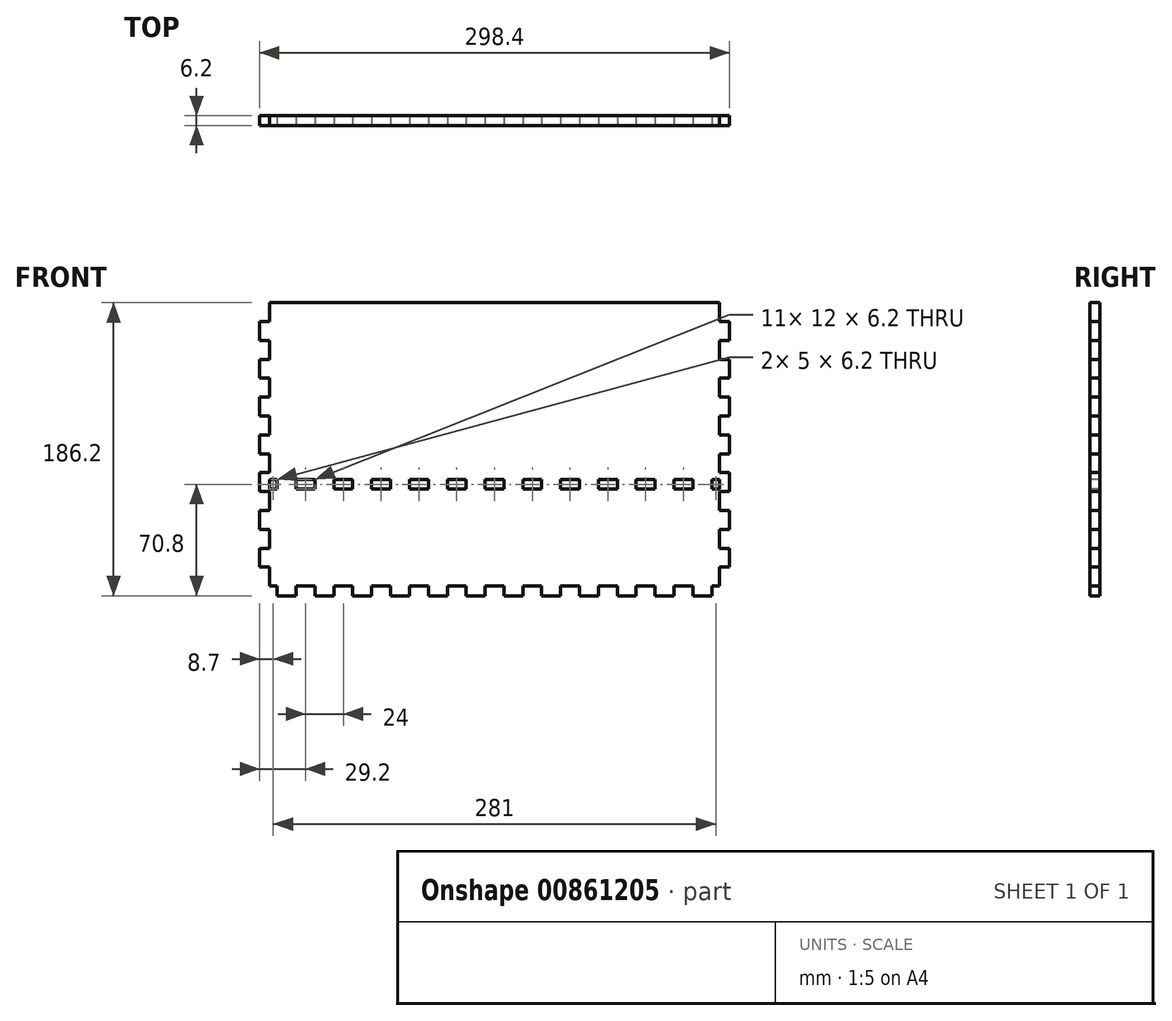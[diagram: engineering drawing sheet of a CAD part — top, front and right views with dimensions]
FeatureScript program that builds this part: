
annotation { "Feature Type Name" : "Feature", "Feature Type Description" : "" }
export const myFeature = defineFeature(function(context is Context, id is Id, definition is map)
    precondition{}
    {
        {
            var Q0;
            Q0=qCreatedBy(makeId("Front.planeOp"),FACE);
            var sketch = newSketch(context, id + "F0", { "sketchPlane" : qUnion([Q0])});
            skLineSegment(sketch, "E0.bottom", {"start": v(143, 90) * mm, "end": v(-143, 90) * mm});
            skLineSegment(sketch, "E0.top", {"start": v(143, -90) * mm, "end": v(-143, -90) * mm});
            skLineSegment(sketch, "E0.left", {"start": v(143, 90) * mm, "end": v(143, -90) * mm});
            skLineSegment(sketch, "E0.right", {"start": v(-143, 90) * mm, "end": v(-143, -90) * mm});
            skPoint(sketch, "E0.middle", {"position": v(0, 0) * mm});
            skSolve(sketch);
        }
        {
            var Q0;
            Q0=makeQuery(id+"F0.imprint","IMPRINT",FACE,{"disambiguationData":[TD([[makeQuery(id+"F0.imprint","IMPRINT",EDGE,{"derivedFrom":sQuery(id+"F0.wireOp",EDGE,"E0.bottom")}),1.0]])]});
            extrude(context, id + "F1", {"entities" : qUnion([Q0]), "depth" : 6.2 * mm, "offsetDistance" : 25 * mm});
        }
        {
            var Q0;
            Q0=makeQuery(id+"F1.opExtrude","CAP_FACE",FACE,{"disambiguationData":[OSD([sQuery(id+"F0.wireOp",EDGE,"E0.bottom"),sQuery(id+"F0.wireOp",EDGE,"E0.top"),sQuery(id+"F0.wireOp",EDGE,"E0.left"),sQuery(id+"F0.wireOp",EDGE,"E0.right")])],"isStart":false});
            var sketch = newSketch(context, id + "F2", { "sketchPlane" : qUnion([Q0])});
            skLineSegment(sketch, "E1", {"start": v(-143, -90) * mm, "end": v(-143, -28.5) * mm, "construction": true});
            skLineSegment(sketch, "E2", {"start": v(-143, -28.5) * mm, "end": v(0, -28.5) * mm, "construction": true});
            skLineSegment(sketch, "E3", {"start": v(0, -28.5) * mm, "end": v(0, -22.3) * mm, "construction": true});
            skLineSegment(sketch, "E4.bottom", {"start": v(6, -22.3) * mm, "end": v(-6, -22.3) * mm});
            skLineSegment(sketch, "E4.top", {"start": v(6, -28.5) * mm, "end": v(-6, -28.5) * mm});
            skLineSegment(sketch, "E4.left", {"start": v(6, -22.3) * mm, "end": v(6, -28.5) * mm});
            skLineSegment(sketch, "E4.right", {"start": v(-6, -22.3) * mm, "end": v(-6, -28.5) * mm});
            skPoint(sketch, "E4.middle", {"position": v(0, -25.4) * mm});
            skLineSegment(sketch, "E5.1.0.0", {"start": v(30, -22.3) * mm, "end": v(18, -22.3) * mm});
            skLineSegment(sketch, "E5.1.0.1", {"start": v(30, -22.3) * mm, "end": v(30, -28.5) * mm});
            skLineSegment(sketch, "E5.1.0.2", {"start": v(30, -28.5) * mm, "end": v(18, -28.5) * mm});
            skLineSegment(sketch, "E5.1.0.3", {"start": v(18, -22.3) * mm, "end": v(18, -28.5) * mm});
            skLineSegment(sketch, "E5.2.0.0", {"start": v(54, -22.3) * mm, "end": v(42, -22.3) * mm});
            skLineSegment(sketch, "E5.2.0.1", {"start": v(54, -22.3) * mm, "end": v(54, -28.5) * mm});
            skLineSegment(sketch, "E5.2.0.2", {"start": v(54, -28.5) * mm, "end": v(42, -28.5) * mm});
            skLineSegment(sketch, "E5.2.0.3", {"start": v(42, -22.3) * mm, "end": v(42, -28.5) * mm});
            skLineSegment(sketch, "E5.3.0.0", {"start": v(78, -22.3) * mm, "end": v(66, -22.3) * mm});
            skLineSegment(sketch, "E5.3.0.1", {"start": v(78, -22.3) * mm, "end": v(78, -28.5) * mm});
            skLineSegment(sketch, "E5.3.0.2", {"start": v(78, -28.5) * mm, "end": v(66, -28.5) * mm});
            skLineSegment(sketch, "E5.3.0.3", {"start": v(66, -22.3) * mm, "end": v(66, -28.5) * mm});
            skLineSegment(sketch, "E5.4.0.0", {"start": v(102, -22.3) * mm, "end": v(90, -22.3) * mm});
            skLineSegment(sketch, "E5.4.0.1", {"start": v(102, -22.3) * mm, "end": v(102, -28.5) * mm});
            skLineSegment(sketch, "E5.4.0.2", {"start": v(102, -28.5) * mm, "end": v(90, -28.5) * mm});
            skLineSegment(sketch, "E5.4.0.3", {"start": v(90, -22.3) * mm, "end": v(90, -28.5) * mm});
            skLineSegment(sketch, "E5.5.0.0", {"start": v(126, -22.3) * mm, "end": v(114, -22.3) * mm});
            skLineSegment(sketch, "E5.5.0.1", {"start": v(126, -22.3) * mm, "end": v(126, -28.5) * mm});
            skLineSegment(sketch, "E5.5.0.2", {"start": v(126, -28.5) * mm, "end": v(114, -28.5) * mm});
            skLineSegment(sketch, "E5.5.0.3", {"start": v(114, -22.3) * mm, "end": v(114, -28.5) * mm});
            skLineSegment(sketch, "E5.direction1", {"start": v(-6, -22.3) * mm, "end": v(18, -22.3) * mm, "construction": true});
            skLineSegment(sketch, "E6.MirrorCS", {"start": v(-78, -22.3) * mm, "end": v(-78, -28.5) * mm});
            skLineSegment(sketch, "E7.MirrorCS", {"start": v(-66, -22.3) * mm, "end": v(-66, -28.5) * mm});
            skLineSegment(sketch, "E8.MirrorCS", {"start": v(-102, -22.3) * mm, "end": v(-102, -28.5) * mm});
            skLineSegment(sketch, "E9.MirrorCS", {"start": v(-90, -22.3) * mm, "end": v(-90, -28.5) * mm});
            skLineSegment(sketch, "E10.MirrorCS", {"start": v(-54, -22.3) * mm, "end": v(-54, -28.5) * mm});
            skLineSegment(sketch, "E11.MirrorCS", {"start": v(-42, -22.3) * mm, "end": v(-42, -28.5) * mm});
            skLineSegment(sketch, "E12.MirrorCS", {"start": v(-126, -22.3) * mm, "end": v(-126, -28.5) * mm});
            skLineSegment(sketch, "E13.MirrorCS", {"start": v(-18, -22.3) * mm, "end": v(-18, -28.5) * mm});
            skLineSegment(sketch, "E14.MirrorCS", {"start": v(-30, -22.3) * mm, "end": v(-30, -28.5) * mm});
            skLineSegment(sketch, "E15.MirrorCS", {"start": v(-114, -22.3) * mm, "end": v(-114, -28.5) * mm});
            skLineSegment(sketch, "E16.MirrorCS", {"start": v(-78, -28.5) * mm, "end": v(-66, -28.5) * mm});
            skLineSegment(sketch, "E17.MirrorCS", {"start": v(-102, -22.3) * mm, "end": v(-90, -22.3) * mm});
            skLineSegment(sketch, "E18.MirrorCS", {"start": v(-102, -28.5) * mm, "end": v(-90, -28.5) * mm});
            skLineSegment(sketch, "E19.MirrorCS", {"start": v(-126, -22.3) * mm, "end": v(-114, -22.3) * mm});
            skLineSegment(sketch, "E20.MirrorCS", {"start": v(-54, -22.3) * mm, "end": v(-42, -22.3) * mm});
            skLineSegment(sketch, "E21.MirrorCS", {"start": v(-54, -28.5) * mm, "end": v(-42, -28.5) * mm});
            skLineSegment(sketch, "E22.MirrorCS", {"start": v(-78, -22.3) * mm, "end": v(-66, -22.3) * mm});
            skLineSegment(sketch, "E23.MirrorCS", {"start": v(-126, -28.5) * mm, "end": v(-114, -28.5) * mm});
            skLineSegment(sketch, "E24.MirrorCS", {"start": v(-30, -22.3) * mm, "end": v(-18, -22.3) * mm});
            skLineSegment(sketch, "E25.MirrorCS", {"start": v(-30, -28.5) * mm, "end": v(-18, -28.5) * mm});
            skLineSegment(sketch, "E26.0.6.0", {"start": v(150, -22.3) * mm, "end": v(138, -22.3) * mm});
            skLineSegment(sketch, "E26.3.6.0", {"start": v(150, -22.3) * mm, "end": v(150, -28.5) * mm});
            skLineSegment(sketch, "E26.6.6.0", {"start": v(150, -28.5) * mm, "end": v(138, -28.5) * mm});
            skLineSegment(sketch, "E26.9.6.0", {"start": v(138, -22.3) * mm, "end": v(138, -28.5) * mm});
            skLineSegment(sketch, "E27.MirrorCS", {"start": v(-150, -22.3) * mm, "end": v(-138, -22.3) * mm});
            skLineSegment(sketch, "E28.MirrorCS", {"start": v(-150, -28.5) * mm, "end": v(-138, -28.5) * mm});
            skLineSegment(sketch, "E29.MirrorCS", {"start": v(-138, -22.3) * mm, "end": v(-138, -28.5) * mm});
            skLineSegment(sketch, "E30.MirrorCS", {"start": v(-150, -22.3) * mm, "end": v(-150, -28.5) * mm});
            skSolve(sketch);
        }
        {
            var Q0;
            Q0=makeQuery(id+"F2.imprint","IMPRINT",FACE,{"disambiguationData":[TD([[makeQuery(id+"F2.imprint","IMPRINT",EDGE,{"derivedFrom":sQuery(id+"F2.wireOp",EDGE,"E12.MirrorCS")}),1.0]])]});
            var Q1;
            Q1=makeQuery(id+"F2.imprint","IMPRINT",FACE,{"disambiguationData":[TD([[makeQuery(id+"F2.imprint","IMPRINT",EDGE,{"derivedFrom":sQuery(id+"F2.wireOp",EDGE,"E8.MirrorCS")}),1.0]])]});
            var Q2;
            Q2=makeQuery(id+"F2.imprint","IMPRINT",FACE,{"disambiguationData":[TD([[makeQuery(id+"F2.imprint","IMPRINT",EDGE,{"derivedFrom":sQuery(id+"F2.wireOp",EDGE,"E6.MirrorCS")}),1.0]])]});
            var Q3;
            Q3=makeQuery(id+"F2.imprint","IMPRINT",FACE,{"disambiguationData":[TD([[makeQuery(id+"F2.imprint","IMPRINT",EDGE,{"derivedFrom":sQuery(id+"F2.wireOp",EDGE,"E10.MirrorCS")}),1.0]])]});
            var Q4;
            Q4=makeQuery(id+"F2.imprint","IMPRINT",FACE,{"disambiguationData":[TD([[makeQuery(id+"F2.imprint","IMPRINT",EDGE,{"derivedFrom":sQuery(id+"F2.wireOp",EDGE,"E13.MirrorCS")}),-1.0]])]});
            var Q5;
            Q5=makeQuery(id+"F2.imprint","IMPRINT",FACE,{"disambiguationData":[TD([[makeQuery(id+"F2.imprint","IMPRINT",EDGE,{"derivedFrom":sQuery(id+"F2.wireOp",EDGE,"E4.bottom")}),1.0]])]});
            var Q6;
            Q6=makeQuery(id+"F2.imprint","IMPRINT",FACE,{"disambiguationData":[TD([[makeQuery(id+"F2.imprint","IMPRINT",EDGE,{"derivedFrom":sQuery(id+"F2.wireOp",EDGE,"E5.1.0.0")}),1.0]])]});
            var Q7;
            Q7=makeQuery(id+"F2.imprint","IMPRINT",FACE,{"disambiguationData":[TD([[makeQuery(id+"F2.imprint","IMPRINT",EDGE,{"derivedFrom":sQuery(id+"F2.wireOp",EDGE,"E5.2.0.0")}),1.0]])]});
            var Q8;
            Q8=makeQuery(id+"F2.imprint","IMPRINT",FACE,{"disambiguationData":[TD([[makeQuery(id+"F2.imprint","IMPRINT",EDGE,{"derivedFrom":sQuery(id+"F2.wireOp",EDGE,"E5.3.0.0")}),1.0]])]});
            var Q9;
            Q9=makeQuery(id+"F2.imprint","IMPRINT",FACE,{"disambiguationData":[TD([[makeQuery(id+"F2.imprint","IMPRINT",EDGE,{"derivedFrom":sQuery(id+"F2.wireOp",EDGE,"E5.4.0.0")}),1.0]])]});
            var Q10;
            Q10=makeQuery(id+"F2.imprint","IMPRINT",FACE,{"disambiguationData":[TD([[makeQuery(id+"F2.imprint","IMPRINT",EDGE,{"derivedFrom":sQuery(id+"F2.wireOp",EDGE,"E5.5.0.0")}),1.0]])]});
            var Q11;
            {var subQ0=sQuery(id+"F2.wireOp",EDGE,"E29.MirrorCS");Q11=makeQuery(id+"F2.imprint","IMPRINT",FACE,{"disambiguationData":[TD([[makeQuery(id+"F2.imprint","IMPRINT",EDGE,{"derivedFrom":subQ0}),-1.0]])]});}
            var Q12;
            {var subQ0=sQuery(id+"F2.wireOp",EDGE,"E26.9.6.0");Q12=makeQuery(id+"F2.imprint","IMPRINT",FACE,{"disambiguationData":[TD([[makeQuery(id+"F2.imprint","IMPRINT",EDGE,{"derivedFrom":subQ0}),1.0]])]});}
            extrude(context, id + "F3", {"entities" : qUnion([Q0, Q1, Q2, Q3, Q4, Q5, Q6, Q7, Q8, Q9, Q10, Q11, Q12]), "operationType" : NewBodyOperationType.REMOVE, "endBound" : BoundingType.THROUGH_ALL, "oppositeDirection" : true, "depth" : 25 * mm, "offsetDistance" : 25 * mm});
        }
        {
            var Q0;
            Q0=makeQuery(id+"F1.opExtrude","CAP_FACE",FACE,{"disambiguationData":[OSD([sQuery(id+"F0.wireOp",EDGE,"E0.bottom"),sQuery(id+"F0.wireOp",EDGE,"E0.top"),sQuery(id+"F0.wireOp",EDGE,"E0.left"),sQuery(id+"F0.wireOp",EDGE,"E0.right")])],"isStart":false});
            var sketch = newSketch(context, id + "F4", { "sketchPlane" : qUnion([Q0])});
            skLineSegment(sketch, "E31", {"start": v(0, -90) * mm, "end": v(6, -90) * mm, "construction": true});
            skLineSegment(sketch, "E32.bottom", {"start": v(6, -90) * mm, "end": v(18, -90) * mm});
            skLineSegment(sketch, "E32.top", {"start": v(6, -96.2) * mm, "end": v(18, -96.2) * mm});
            skLineSegment(sketch, "E32.left", {"start": v(6, -90) * mm, "end": v(6, -96.2) * mm});
            skLineSegment(sketch, "E32.right", {"start": v(18, -90) * mm, "end": v(18, -96.2) * mm});
            skLineSegment(sketch, "E33.1.0.0", {"start": v(30, -96.2) * mm, "end": v(42, -96.2) * mm});
            skLineSegment(sketch, "E33.1.0.1", {"start": v(42, -90) * mm, "end": v(42, -96.2) * mm});
            skLineSegment(sketch, "E33.1.0.2", {"start": v(30, -90) * mm, "end": v(42, -90) * mm});
            skLineSegment(sketch, "E33.1.0.3", {"start": v(30, -90) * mm, "end": v(30, -96.2) * mm});
            skLineSegment(sketch, "E33.1.0.4", {"start": v(24, -90) * mm, "end": v(30, -90) * mm, "construction": true});
            skLineSegment(sketch, "E33.2.0.0", {"start": v(54, -96.2) * mm, "end": v(66, -96.2) * mm});
            skLineSegment(sketch, "E33.2.0.1", {"start": v(66, -90) * mm, "end": v(66, -96.2) * mm});
            skLineSegment(sketch, "E33.2.0.2", {"start": v(54, -90) * mm, "end": v(66, -90) * mm});
            skLineSegment(sketch, "E33.2.0.3", {"start": v(54, -90) * mm, "end": v(54, -96.2) * mm});
            skLineSegment(sketch, "E33.2.0.4", {"start": v(48, -90) * mm, "end": v(54, -90) * mm, "construction": true});
            skLineSegment(sketch, "E33.3.0.0", {"start": v(78, -96.2) * mm, "end": v(90, -96.2) * mm});
            skLineSegment(sketch, "E33.3.0.1", {"start": v(90, -90) * mm, "end": v(90, -96.2) * mm});
            skLineSegment(sketch, "E33.3.0.2", {"start": v(78, -90) * mm, "end": v(90, -90) * mm});
            skLineSegment(sketch, "E33.3.0.3", {"start": v(78, -90) * mm, "end": v(78, -96.2) * mm});
            skLineSegment(sketch, "E33.3.0.4", {"start": v(72, -90) * mm, "end": v(78, -90) * mm, "construction": true});
            skLineSegment(sketch, "E33.4.0.0", {"start": v(102, -96.2) * mm, "end": v(114, -96.2) * mm});
            skLineSegment(sketch, "E33.4.0.1", {"start": v(114, -90) * mm, "end": v(114, -96.2) * mm});
            skLineSegment(sketch, "E33.4.0.2", {"start": v(102, -90) * mm, "end": v(114, -90) * mm});
            skLineSegment(sketch, "E33.4.0.3", {"start": v(102, -90) * mm, "end": v(102, -96.2) * mm});
            skLineSegment(sketch, "E33.4.0.4", {"start": v(96, -90) * mm, "end": v(102, -90) * mm, "construction": true});
            skLineSegment(sketch, "E33.5.0.0", {"start": v(126, -96.2) * mm, "end": v(138, -96.2) * mm});
            skLineSegment(sketch, "E33.5.0.1", {"start": v(138, -90) * mm, "end": v(138, -96.2) * mm});
            skLineSegment(sketch, "E33.5.0.2", {"start": v(126, -90) * mm, "end": v(138, -90) * mm});
            skLineSegment(sketch, "E33.5.0.3", {"start": v(126, -90) * mm, "end": v(126, -96.2) * mm});
            skLineSegment(sketch, "E33.5.0.4", {"start": v(120, -90) * mm, "end": v(126, -90) * mm, "construction": true});
            skLineSegment(sketch, "E33.direction1", {"start": v(6, -96.2) * mm, "end": v(30, -96.2) * mm, "construction": true});
            skLineSegment(sketch, "E34.MirrorCS", {"start": v(-6, -90) * mm, "end": v(-6, -96.2) * mm});
            skLineSegment(sketch, "E35.MirrorCS", {"start": v(-30, -90) * mm, "end": v(-30, -96.2) * mm});
            skLineSegment(sketch, "E36.MirrorCS", {"start": v(-42, -90) * mm, "end": v(-42, -96.2) * mm});
            skLineSegment(sketch, "E37.MirrorCS", {"start": v(-78, -90) * mm, "end": v(-78, -96.2) * mm});
            skLineSegment(sketch, "E38.MirrorCS", {"start": v(-18, -90) * mm, "end": v(-18, -96.2) * mm});
            skLineSegment(sketch, "E39.MirrorCS", {"start": v(-114, -90) * mm, "end": v(-114, -96.2) * mm});
            skLineSegment(sketch, "E40.MirrorCS", {"start": v(-102, -90) * mm, "end": v(-102, -96.2) * mm});
            skLineSegment(sketch, "E41.MirrorCS", {"start": v(-66, -90) * mm, "end": v(-66, -96.2) * mm});
            skLineSegment(sketch, "E42.MirrorCS", {"start": v(-54, -90) * mm, "end": v(-54, -96.2) * mm});
            skLineSegment(sketch, "E43.MirrorCS", {"start": v(-138, -90) * mm, "end": v(-138, -96.2) * mm});
            skLineSegment(sketch, "E44.MirrorCS", {"start": v(-126, -90) * mm, "end": v(-126, -96.2) * mm});
            skLineSegment(sketch, "E45.MirrorCS", {"start": v(-90, -90) * mm, "end": v(-90, -96.2) * mm});
            skLineSegment(sketch, "E46.MirrorCS", {"start": v(-72, -90) * mm, "end": v(-78, -90) * mm, "construction": true});
            skLineSegment(sketch, "E47.MirrorCS", {"start": v(-120, -90) * mm, "end": v(-126, -90) * mm, "construction": true});
            skLineSegment(sketch, "E48.MirrorCS", {"start": v(-6, -96.2) * mm, "end": v(-18, -96.2) * mm});
            skLineSegment(sketch, "E49.MirrorCS", {"start": v(-96, -90) * mm, "end": v(-102, -90) * mm, "construction": true});
            skLineSegment(sketch, "E50.MirrorCS", {"start": v(-48, -90) * mm, "end": v(-54, -90) * mm, "construction": true});
            skLineSegment(sketch, "E51.MirrorCS", {"start": v(-24, -90) * mm, "end": v(-30, -90) * mm, "construction": true});
            skLineSegment(sketch, "E52.MirrorCS", {"start": v(-78, -90) * mm, "end": v(-90, -90) * mm});
            skLineSegment(sketch, "E53.MirrorCS", {"start": v(-30, -96.2) * mm, "end": v(-42, -96.2) * mm});
            skLineSegment(sketch, "E54.MirrorCS", {"start": v(-102, -96.2) * mm, "end": v(-114, -96.2) * mm});
            skLineSegment(sketch, "E55.MirrorCS", {"start": v(-6, -96.2) * mm, "end": v(-30, -96.2) * mm, "construction": true});
            skLineSegment(sketch, "E56.MirrorCS", {"start": v(-6, -90) * mm, "end": v(-18, -90) * mm});
            skLineSegment(sketch, "E57.MirrorCS", {"start": v(-102, -90) * mm, "end": v(-114, -90) * mm});
            skLineSegment(sketch, "E58.MirrorCS", {"start": v(-54, -90) * mm, "end": v(-66, -90) * mm});
            skLineSegment(sketch, "E59.MirrorCS", {"start": v(-126, -96.2) * mm, "end": v(-138, -96.2) * mm});
            skLineSegment(sketch, "E60.MirrorCS", {"start": v(-54, -96.2) * mm, "end": v(-66, -96.2) * mm});
            skLineSegment(sketch, "E61.MirrorCS", {"start": v(-126, -90) * mm, "end": v(-138, -90) * mm});
            skLineSegment(sketch, "E62.MirrorCS", {"start": v(-78, -96.2) * mm, "end": v(-90, -96.2) * mm});
            skLineSegment(sketch, "E63.MirrorCS", {"start": v(-30, -90) * mm, "end": v(-42, -90) * mm});
            skSolve(sketch);
        }
        {
            var Q0;
            Q0=makeQuery(id+"F4.imprint","IMPRINT",FACE,{"disambiguationData":[TD([[makeQuery(id+"F4.imprint","IMPRINT",EDGE,{"derivedFrom":sQuery(id+"F4.wireOp",EDGE,"E43.MirrorCS")}),1.0]])]});
            var Q1;
            Q1=makeQuery(id+"F4.imprint","IMPRINT",FACE,{"disambiguationData":[TD([[makeQuery(id+"F4.imprint","IMPRINT",EDGE,{"derivedFrom":sQuery(id+"F4.wireOp",EDGE,"E39.MirrorCS")}),1.0]])]});
            var Q2;
            Q2=makeQuery(id+"F4.imprint","IMPRINT",FACE,{"disambiguationData":[TD([[makeQuery(id+"F4.imprint","IMPRINT",EDGE,{"derivedFrom":sQuery(id+"F4.wireOp",EDGE,"E37.MirrorCS")}),-1.0]])]});
            var Q3;
            Q3=makeQuery(id+"F4.imprint","IMPRINT",FACE,{"disambiguationData":[TD([[makeQuery(id+"F4.imprint","IMPRINT",EDGE,{"derivedFrom":sQuery(id+"F4.wireOp",EDGE,"E41.MirrorCS")}),1.0]])]});
            var Q4;
            Q4=makeQuery(id+"F4.imprint","IMPRINT",FACE,{"disambiguationData":[TD([[makeQuery(id+"F4.imprint","IMPRINT",EDGE,{"derivedFrom":sQuery(id+"F4.wireOp",EDGE,"E35.MirrorCS")}),-1.0]])]});
            var Q5;
            Q5=makeQuery(id+"F4.imprint","IMPRINT",FACE,{"disambiguationData":[TD([[makeQuery(id+"F4.imprint","IMPRINT",EDGE,{"derivedFrom":sQuery(id+"F4.wireOp",EDGE,"E34.MirrorCS")}),-1.0]])]});
            var Q6;
            Q6=makeQuery(id+"F4.imprint","IMPRINT",FACE,{"disambiguationData":[TD([[makeQuery(id+"F4.imprint","IMPRINT",EDGE,{"derivedFrom":sQuery(id+"F4.wireOp",EDGE,"E32.bottom")}),1.0]])]});
            var Q7;
            Q7=makeQuery(id+"F4.imprint","IMPRINT",FACE,{"disambiguationData":[TD([[makeQuery(id+"F4.imprint","IMPRINT",EDGE,{"derivedFrom":sQuery(id+"F4.wireOp",EDGE,"E33.1.0.0")}),1.0]])]});
            var Q8;
            Q8=makeQuery(id+"F4.imprint","IMPRINT",FACE,{"disambiguationData":[TD([[makeQuery(id+"F4.imprint","IMPRINT",EDGE,{"derivedFrom":sQuery(id+"F4.wireOp",EDGE,"E33.2.0.0")}),1.0]])]});
            var Q9;
            Q9=makeQuery(id+"F4.imprint","IMPRINT",FACE,{"disambiguationData":[TD([[makeQuery(id+"F4.imprint","IMPRINT",EDGE,{"derivedFrom":sQuery(id+"F4.wireOp",EDGE,"E33.3.0.0")}),1.0]])]});
            var Q10;
            Q10=makeQuery(id+"F4.imprint","IMPRINT",FACE,{"disambiguationData":[TD([[makeQuery(id+"F4.imprint","IMPRINT",EDGE,{"derivedFrom":sQuery(id+"F4.wireOp",EDGE,"E33.4.0.0")}),1.0]])]});
            var Q11;
            Q11=makeQuery(id+"F4.imprint","IMPRINT",FACE,{"disambiguationData":[TD([[makeQuery(id+"F4.imprint","IMPRINT",EDGE,{"derivedFrom":sQuery(id+"F4.wireOp",EDGE,"E33.5.0.0")}),1.0]])]});
            var Q12;
            Q12=makeQuery(id+"F1.opExtrude","CAP_FACE",FACE,{"disambiguationData":[OSD([sQuery(id+"F0.wireOp",EDGE,"E0.bottom"),sQuery(id+"F0.wireOp",EDGE,"E0.top"),sQuery(id+"F0.wireOp",EDGE,"E0.left"),sQuery(id+"F0.wireOp",EDGE,"E0.right")])],"isStart":true});
            extrude(context, id + "F5", {"entities" : qUnion([Q0, Q1, Q2, Q3, Q4, Q5, Q6, Q7, Q8, Q9, Q10, Q11]), "operationType" : NewBodyOperationType.ADD, "endBound" : BoundingType.UP_TO_SURFACE, "oppositeDirection" : true, "depth" : 25 * mm, "endBoundEntityFace" : qUnion([Q12]), "offsetDistance" : 25 * mm});
        }
        {
            var Q0;
            Q0=makeQuery(id+"F5.boolean.opBoolean","MERGE",FACE,{"derivedFrom":[makeQuery(id+"F1.opExtrude","CAP_FACE",FACE,{"disambiguationData":[OSD([sQuery(id+"F0.wireOp",EDGE,"E0.bottom"),sQuery(id+"F0.wireOp",EDGE,"E0.top"),sQuery(id+"F0.wireOp",EDGE,"E0.left"),sQuery(id+"F0.wireOp",EDGE,"E0.right")])],"isStart":false}),makeQuery(id+"F5.opExtrude","CAP_FACE",FACE,{"disambiguationData":[OSD([sQuery(id+"F4.wireOp",EDGE,"E32.bottom"),sQuery(id+"F4.wireOp",EDGE,"E32.top"),sQuery(id+"F4.wireOp",EDGE,"E32.left"),sQuery(id+"F4.wireOp",EDGE,"E32.right")])],"isStart":true}),makeQuery(id+"F5.opExtrude","CAP_FACE",FACE,{"disambiguationData":[OSD([sQuery(id+"F4.wireOp",EDGE,"E33.1.0.0"),sQuery(id+"F4.wireOp",EDGE,"E33.1.0.1"),sQuery(id+"F4.wireOp",EDGE,"E33.1.0.2"),sQuery(id+"F4.wireOp",EDGE,"E33.1.0.3")])],"isStart":true}),makeQuery(id+"F5.opExtrude","CAP_FACE",FACE,{"disambiguationData":[OSD([sQuery(id+"F4.wireOp",EDGE,"E33.2.0.0"),sQuery(id+"F4.wireOp",EDGE,"E33.2.0.1"),sQuery(id+"F4.wireOp",EDGE,"E33.2.0.2"),sQuery(id+"F4.wireOp",EDGE,"E33.2.0.3")])],"isStart":true}),makeQuery(id+"F5.opExtrude","CAP_FACE",FACE,{"disambiguationData":[OSD([sQuery(id+"F4.wireOp",EDGE,"E33.3.0.0"),sQuery(id+"F4.wireOp",EDGE,"E33.3.0.1"),sQuery(id+"F4.wireOp",EDGE,"E33.3.0.2"),sQuery(id+"F4.wireOp",EDGE,"E33.3.0.3")])],"isStart":true}),makeQuery(id+"F5.opExtrude","CAP_FACE",FACE,{"disambiguationData":[OSD([sQuery(id+"F4.wireOp",EDGE,"E33.4.0.0"),sQuery(id+"F4.wireOp",EDGE,"E33.4.0.1"),sQuery(id+"F4.wireOp",EDGE,"E33.4.0.2"),sQuery(id+"F4.wireOp",EDGE,"E33.4.0.3")])],"isStart":true}),makeQuery(id+"F5.opExtrude","CAP_FACE",FACE,{"disambiguationData":[OSD([sQuery(id+"F4.wireOp",EDGE,"E33.5.0.0"),sQuery(id+"F4.wireOp",EDGE,"E33.5.0.1"),sQuery(id+"F4.wireOp",EDGE,"E33.5.0.2"),sQuery(id+"F4.wireOp",EDGE,"E33.5.0.3")])],"isStart":true}),makeQuery(id+"F5.opExtrude","CAP_FACE",FACE,{"disambiguationData":[OSD([sQuery(id+"F4.wireOp",EDGE,"E34.MirrorCS"),sQuery(id+"F4.wireOp",EDGE,"E38.MirrorCS"),sQuery(id+"F4.wireOp",EDGE,"E48.MirrorCS"),sQuery(id+"F4.wireOp",EDGE,"E56.MirrorCS")])],"isStart":true}),makeQuery(id+"F5.opExtrude","CAP_FACE",FACE,{"disambiguationData":[OSD([sQuery(id+"F4.wireOp",EDGE,"E35.MirrorCS"),sQuery(id+"F4.wireOp",EDGE,"E36.MirrorCS"),sQuery(id+"F4.wireOp",EDGE,"E53.MirrorCS"),sQuery(id+"F4.wireOp",EDGE,"E63.MirrorCS")])],"isStart":true}),makeQuery(id+"F5.opExtrude","CAP_FACE",FACE,{"disambiguationData":[OSD([sQuery(id+"F4.wireOp",EDGE,"E37.MirrorCS"),sQuery(id+"F4.wireOp",EDGE,"E45.MirrorCS"),sQuery(id+"F4.wireOp",EDGE,"E52.MirrorCS"),sQuery(id+"F4.wireOp",EDGE,"E62.MirrorCS")])],"isStart":true}),makeQuery(id+"F5.opExtrude","CAP_FACE",FACE,{"disambiguationData":[OSD([sQuery(id+"F4.wireOp",EDGE,"E39.MirrorCS"),sQuery(id+"F4.wireOp",EDGE,"E40.MirrorCS"),sQuery(id+"F4.wireOp",EDGE,"E54.MirrorCS"),sQuery(id+"F4.wireOp",EDGE,"E57.MirrorCS")])],"isStart":true}),makeQuery(id+"F5.opExtrude","CAP_FACE",FACE,{"disambiguationData":[OSD([sQuery(id+"F4.wireOp",EDGE,"E41.MirrorCS"),sQuery(id+"F4.wireOp",EDGE,"E42.MirrorCS"),sQuery(id+"F4.wireOp",EDGE,"E58.MirrorCS"),sQuery(id+"F4.wireOp",EDGE,"E60.MirrorCS")])],"isStart":true}),makeQuery(id+"F5.opExtrude","CAP_FACE",FACE,{"disambiguationData":[OSD([sQuery(id+"F4.wireOp",EDGE,"E43.MirrorCS"),sQuery(id+"F4.wireOp",EDGE,"E44.MirrorCS"),sQuery(id+"F4.wireOp",EDGE,"E59.MirrorCS"),sQuery(id+"F4.wireOp",EDGE,"E61.MirrorCS")])],"isStart":true})]});
            var sketch = newSketch(context, id + "F6", { "sketchPlane" : qUnion([Q0])});
            skLineSegment(sketch, "E64", {"start": v(0, 0) * mm, "end": v(-143, 0) * mm, "construction": true});
            skLineSegment(sketch, "E65", {"start": v(-143, 0) * mm, "end": v(-149.2, 0) * mm, "construction": true});
            skLineSegment(sketch, "E66.bottom", {"start": v(-149.2, 6) * mm, "end": v(-143, 6) * mm});
            skLineSegment(sketch, "E66.top", {"start": v(-149.2, -6) * mm, "end": v(-143, -6) * mm});
            skLineSegment(sketch, "E66.left", {"start": v(-149.2, 6) * mm, "end": v(-149.2, -6) * mm});
            skLineSegment(sketch, "E66.right", {"start": v(-143, 6) * mm, "end": v(-143, -6) * mm});
            skPoint(sketch, "E66.middle", {"position": v(-146.1, 0) * mm});
            skLineSegment(sketch, "E67.0.1.0", {"start": v(-149.2, 30) * mm, "end": v(-143, 30) * mm});
            skLineSegment(sketch, "E67.0.1.1", {"start": v(-143, 30) * mm, "end": v(-143, 18) * mm});
            skLineSegment(sketch, "E67.0.1.2", {"start": v(-149.2, 30) * mm, "end": v(-149.2, 18) * mm});
            skLineSegment(sketch, "E67.0.1.3", {"start": v(-149.2, 18) * mm, "end": v(-143, 18) * mm});
            skLineSegment(sketch, "E67.0.2.0", {"start": v(-149.2, 54) * mm, "end": v(-143, 54) * mm});
            skLineSegment(sketch, "E67.0.2.1", {"start": v(-143, 54) * mm, "end": v(-143, 42) * mm});
            skLineSegment(sketch, "E67.0.2.2", {"start": v(-149.2, 54) * mm, "end": v(-149.2, 42) * mm});
            skLineSegment(sketch, "E67.0.2.3", {"start": v(-149.2, 42) * mm, "end": v(-143, 42) * mm});
            skLineSegment(sketch, "E67.0.3.0", {"start": v(-149.2, 78) * mm, "end": v(-143, 78) * mm});
            skLineSegment(sketch, "E67.0.3.1", {"start": v(-143, 78) * mm, "end": v(-143, 66) * mm});
            skLineSegment(sketch, "E67.0.3.2", {"start": v(-149.2, 78) * mm, "end": v(-149.2, 66) * mm});
            skLineSegment(sketch, "E67.0.3.3", {"start": v(-149.2, 66) * mm, "end": v(-143, 66) * mm});
            skLineSegment(sketch, "E67.direction1", {"start": v(-149.2, 6) * mm, "end": v(-124.2, 6) * mm, "construction": true});
            skLineSegment(sketch, "E67.direction2", {"start": v(-149.2, 6) * mm, "end": v(-149.2, 30) * mm, "construction": true});
            skLineSegment(sketch, "E68.MirrorCS", {"start": v(-149.2, -30) * mm, "end": v(-143, -30) * mm});
            skLineSegment(sketch, "E69.MirrorCS", {"start": v(-143, -30) * mm, "end": v(-143, -18) * mm});
            skLineSegment(sketch, "E70.MirrorCS", {"start": v(-149.2, -54) * mm, "end": v(-149.2, -42) * mm});
            skLineSegment(sketch, "E71.MirrorCS", {"start": v(-149.2, -78) * mm, "end": v(-143, -78) * mm});
            skLineSegment(sketch, "E72.MirrorCS", {"start": v(-143, -54) * mm, "end": v(-143, -42) * mm});
            skLineSegment(sketch, "E73.MirrorCS", {"start": v(-149.2, -42) * mm, "end": v(-143, -42) * mm});
            skLineSegment(sketch, "E74.MirrorCS", {"start": v(-149.2, -18) * mm, "end": v(-143, -18) * mm});
            skLineSegment(sketch, "E75.MirrorCS", {"start": v(-149.2, -30) * mm, "end": v(-149.2, -18) * mm});
            skLineSegment(sketch, "E76.MirrorCS", {"start": v(-149.2, -66) * mm, "end": v(-143, -66) * mm});
            skLineSegment(sketch, "E77.MirrorCS", {"start": v(-149.2, -54) * mm, "end": v(-143, -54) * mm});
            skLineSegment(sketch, "E78.MirrorCS", {"start": v(-149.2, -78) * mm, "end": v(-149.2, -66) * mm});
            skLineSegment(sketch, "E79.MirrorCS", {"start": v(-143, -78) * mm, "end": v(-143, -66) * mm});
            skLineSegment(sketch, "E80.MirrorCS", {"start": v(149.2, 6) * mm, "end": v(143, 6) * mm});
            skLineSegment(sketch, "E81.MirrorCS", {"start": v(143, 6) * mm, "end": v(143, -6) * mm});
            skLineSegment(sketch, "E82.MirrorCS", {"start": v(149.2, 6) * mm, "end": v(149.2, -6) * mm});
            skLineSegment(sketch, "E83.MirrorCS", {"start": v(143, 0) * mm, "end": v(149.2, 0) * mm, "construction": true});
            skLineSegment(sketch, "E84.MirrorCS", {"start": v(149.2, 30) * mm, "end": v(143, 30) * mm});
            skLineSegment(sketch, "E85.MirrorCS", {"start": v(149.2, 30) * mm, "end": v(149.2, 18) * mm});
            skLineSegment(sketch, "E86.MirrorCS", {"start": v(149.2, -6) * mm, "end": v(143, -6) * mm});
            skLineSegment(sketch, "E87.MirrorCS", {"start": v(149.2, -18) * mm, "end": v(143, -18) * mm});
            skLineSegment(sketch, "E88.MirrorCS", {"start": v(143, 30) * mm, "end": v(143, 18) * mm});
            skLineSegment(sketch, "E89.MirrorCS", {"start": v(149.2, 6) * mm, "end": v(149.2, 30) * mm, "construction": true});
            skLineSegment(sketch, "E90.MirrorCS", {"start": v(143, -78) * mm, "end": v(143, -66) * mm});
            skLineSegment(sketch, "E91.MirrorCS", {"start": v(149.2, -30) * mm, "end": v(143, -30) * mm});
            skLineSegment(sketch, "E92.MirrorCS", {"start": v(149.2, -54) * mm, "end": v(149.2, -42) * mm});
            skLineSegment(sketch, "E93.MirrorCS", {"start": v(149.2, -78) * mm, "end": v(143, -78) * mm});
            skLineSegment(sketch, "E94.MirrorCS", {"start": v(149.2, 18) * mm, "end": v(143, 18) * mm});
            skLineSegment(sketch, "E95.MirrorCS", {"start": v(149.2, 78) * mm, "end": v(149.2, 66) * mm});
            skLineSegment(sketch, "E96.MirrorCS", {"start": v(149.2, 66) * mm, "end": v(143, 66) * mm});
            skLineSegment(sketch, "E97.MirrorCS", {"start": v(149.2, 54) * mm, "end": v(143, 54) * mm});
            skLineSegment(sketch, "E98.MirrorCS", {"start": v(149.2, -66) * mm, "end": v(143, -66) * mm});
            skLineSegment(sketch, "E99.MirrorCS", {"start": v(143, 54) * mm, "end": v(143, 42) * mm});
            skLineSegment(sketch, "E100.MirrorCS", {"start": v(149.2, -42) * mm, "end": v(143, -42) * mm});
            skLineSegment(sketch, "E101.MirrorCS", {"start": v(149.2, 54) * mm, "end": v(149.2, 42) * mm});
            skLineSegment(sketch, "E102.MirrorCS", {"start": v(149.2, 42) * mm, "end": v(143, 42) * mm});
            skLineSegment(sketch, "E103.MirrorCS", {"start": v(149.2, 78) * mm, "end": v(143, 78) * mm});
            skLineSegment(sketch, "E104.MirrorCS", {"start": v(143, -30) * mm, "end": v(143, -18) * mm});
            skLineSegment(sketch, "E105.MirrorCS", {"start": v(143, -54) * mm, "end": v(143, -42) * mm});
            skLineSegment(sketch, "E106.MirrorCS", {"start": v(149.2, -54) * mm, "end": v(143, -54) * mm});
            skLineSegment(sketch, "E107.MirrorCS", {"start": v(149.2, -30) * mm, "end": v(149.2, -18) * mm});
            skLineSegment(sketch, "E108.MirrorCS", {"start": v(149.2, -78) * mm, "end": v(149.2, -66) * mm});
            skLineSegment(sketch, "E109.MirrorCS", {"start": v(143, 78) * mm, "end": v(143, 66) * mm});
            skLineSegment(sketch, "E110.MirrorCS", {"start": v(149.2, 6) * mm, "end": v(124.2, 6) * mm, "construction": true});
            skPoint(sketch, "E111.MirrorP", {"position": v(146.1, 0) * mm});
            skSolve(sketch);
        }
        {
            var Q0;
            Q0 = qSketchRegion(id + "F6", true);
            extrude(context, id + "F7", {"entities" : qUnion([Q0]), "operationType" : NewBodyOperationType.ADD, "oppositeDirection" : true, "depth" : 6.2 * mm, "offsetDistance" : 25 * mm});
        }
    });
